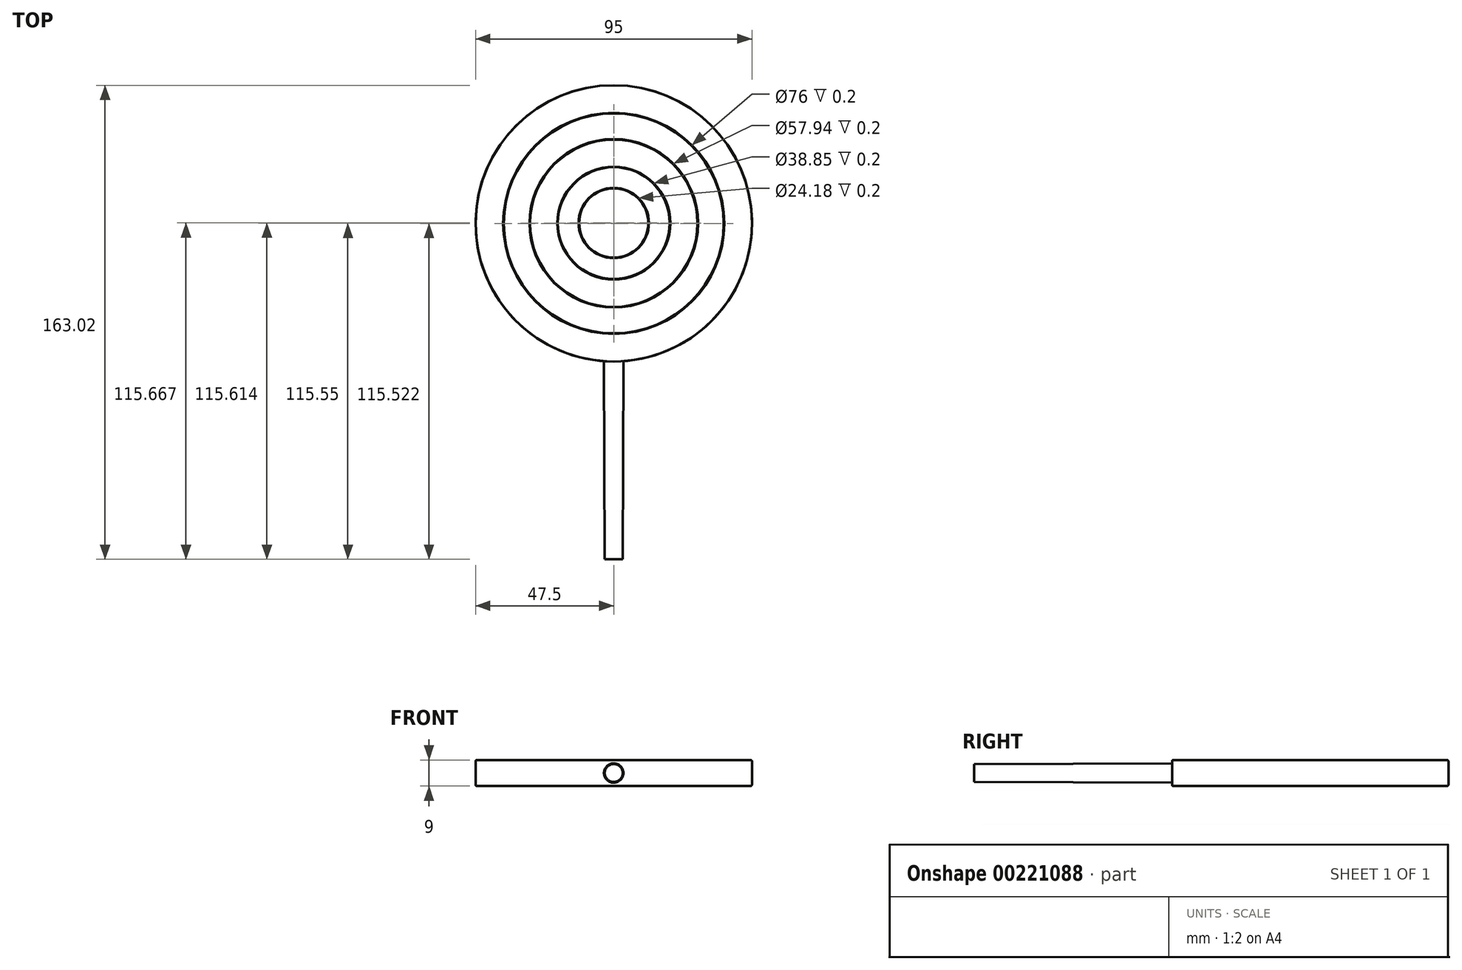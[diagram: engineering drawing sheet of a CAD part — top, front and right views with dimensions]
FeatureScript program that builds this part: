
annotation { "Feature Type Name" : "Feature", "Feature Type Description" : "" }
export const myFeature = defineFeature(function(context is Context, id is Id, definition is map)
    precondition{}
    {
        {
            var Q0;
            Q0=qCreatedBy(makeId("Front.planeOp"),FACE);
            var sketch = newSketch(context, id + "F0", { "sketchPlane" : qUnion([Q0])});
            skCircle(sketch, "E0", {"center": v(0, 1.52) * mm, "radius": 47.5 * mm});
            skLineSegment(sketch, "E1.bottom", {"start": v(35, -115.53) * mm, "end": v(-35, -115.53) * mm});
            skLineSegment(sketch, "E1.top", {"start": v(35, -84.47) * mm, "end": v(-35, -84.47) * mm});
            skLineSegment(sketch, "E1.left", {"start": v(35, -115.53) * mm, "end": v(35, -84.47) * mm});
            skLineSegment(sketch, "E1.right", {"start": v(-35, -115.53) * mm, "end": v(-35, -84.47) * mm});
            skPoint(sketch, "E1.middle", {"position": v(0, -100) * mm});
            skLineSegment(sketch, "E2", {"start": v(0, 71.57) * mm, "end": v(0, -130.11) * mm, "construction": true});
            skPoint(sketch, "E2.endSnap0", {"position": v(0, -115.53) * mm});
            skSolve(sketch);
        }
        {
            var Q0;
            Q0=makeQuery(id+"F0.imprint","IMPRINT",FACE,{"disambiguationData":[TD([[makeQuery(id+"F0.imprint","IMPRINT",EDGE,{"derivedFrom":sQuery(id+"F0.wireOp",EDGE,"E0")}),1.0]])]});
            var Q1;
            Q1=sQuery(id+"F0.wireOp",EDGE,"E0");
            extrude(context, id + "F1", {"entities" : qUnion([Q0]), "surfaceEntities" : qUnion([Q1]), "endBound" : BoundingType.SYMMETRIC, "depth" : 9 * mm});
        }
        {
            var Q0;
            Q0=qCreatedBy(makeId("Top.planeOp"),FACE);
            var sketch = newSketch(context, id + "F2", { "sketchPlane" : qUnion([Q0])});
            skCircle(sketch, "E3", {"center": v(0, 0) * mm, "radius": 3.5 * mm});
            skSolve(sketch);
        }
        {
            var Q0;
            Q0=qSketchRegion(id+"F2",true);
            extrude(context, id + "F3", {"entities" : qUnion([Q0]), "operationType" : NewBodyOperationType.ADD, "oppositeDirection" : true, "depth" : 114 * mm, "hasDraft" : true, "draftAngle" : 0.2 * degree, "draftPullDirection" : true});
        }
        {
            var Q0;
            Q0=makeQuery(id+"F1.opExtrude","CAP_EDGE",EDGE,{"disambiguationData":[OSD([sQuery(id+"F0.wireOp",EDGE,"E0")])],"isStart":false});
            var Q1;
            Q1=makeQuery(id+"F1.opExtrude","CAP_EDGE",EDGE,{"disambiguationData":[OSD([sQuery(id+"F0.wireOp",EDGE,"E0")])],"isStart":true});
            fillet(context, id + "F4", {"entities" : qUnion([Q0, Q1]), "radius" : 0.5 * mm, "tangentPropagation" : true, "allowEdgeOverflow" : false});
        }
        {
            var Q0;
            Q0=makeQuery(id+"F1.opExtrude","CAP_FACE",FACE,{"disambiguationData":[OSD([sQuery(id+"F0.wireOp",EDGE,"E0")])],"isStart":false});
            var sketch = newSketch(context, id + "F5", { "sketchPlane" : qUnion([Q0])});
            skCircle(sketch, "E4", {"center": v(0, 1.52) * mm, "radius": 37.8 * mm});
            skCircle(sketch, "E5.0", {"center": v(0, 1.52) * mm, "radius": 38 * mm});
            skSolve(sketch);
        }
        {
            var Q0;
            Q0=qSketchRegion(id+"F5",true);
            extrude(context, id + "F6", {"entities" : qUnion([Q0]), "operationType" : NewBodyOperationType.REMOVE, "oppositeDirection" : true, "depth" : 0.2 * mm});
        }
        {
            var Q0;
            Q0=makeQuery(id+"F5.imprint","IMPRINT",FACE,{"disambiguationData":[TD([[makeQuery(id+"F5.imprint","IMPRINT",EDGE,{"derivedFrom":sQuery(id+"F5.wireOp",EDGE,"E5.0")}),-1.0]])]});
            var sketch = newSketch(context, id + "F7", { "sketchPlane" : qUnion([Q0])});
            skCircle(sketch, "E6", {"center": v(0, 1.55) * mm, "radius": 28.77 * mm});
            skCircle(sketch, "E7.0", {"center": v(0, 1.55) * mm, "radius": 28.97 * mm});
            skSolve(sketch);
        }
        {
            var Q0;
            Q0=qSketchRegion(id+"F7",true);
            extrude(context, id + "F8", {"entities" : qUnion([Q0]), "operationType" : NewBodyOperationType.REMOVE, "oppositeDirection" : true, "depth" : 0.2 * mm});
        }
        {
            var Q0;
            Q0=makeQuery(id+"F5.imprint","IMPRINT",FACE,{"disambiguationData":[TD([[makeQuery(id+"F5.imprint","IMPRINT",EDGE,{"derivedFrom":sQuery(id+"F5.wireOp",EDGE,"E5.0")}),-1.0]])]});
            var sketch = newSketch(context, id + "F9", { "sketchPlane" : qUnion([Q0])});
            skCircle(sketch, "E8", {"center": v(0, 1.61) * mm, "radius": 19.23 * mm});
            skCircle(sketch, "E9.0", {"center": v(0, 1.61) * mm, "radius": 19.43 * mm});
            skSolve(sketch);
        }
        {
            var Q0;
            Q0=qSketchRegion(id+"F9",true);
            extrude(context, id + "F10", {"entities" : qUnion([Q0]), "operationType" : NewBodyOperationType.REMOVE, "oppositeDirection" : true, "depth" : 0.2 * mm});
        }
        {
            var Q0;
            Q0=makeQuery(id+"F5.imprint","IMPRINT",FACE,{"disambiguationData":[TD([[makeQuery(id+"F5.imprint","IMPRINT",EDGE,{"derivedFrom":sQuery(id+"F5.wireOp",EDGE,"E5.0")}),-1.0]])]});
            var sketch = newSketch(context, id + "F11", { "sketchPlane" : qUnion([Q0])});
            skCircle(sketch, "E10", {"center": v(0, 1.67) * mm, "radius": 11.89 * mm});
            skCircle(sketch, "E11.0", {"center": v(0, 1.67) * mm, "radius": 12.09 * mm});
            skSolve(sketch);
        }
        {
            var Q0;
            Q0=makeQuery(id+"F11.imprint","IMPRINT",FACE,{"disambiguationData":[TD([[makeQuery(id+"F11.imprint","IMPRINT",EDGE,{"derivedFrom":sQuery(id+"F11.wireOp",EDGE,"E10")}),-1.0]])]});
            extrude(context, id + "F12", {"entities" : qUnion([Q0]), "operationType" : NewBodyOperationType.REMOVE, "oppositeDirection" : true, "depth" : 0.2 * mm});
        }
        {
            var Q0;
            Q0=qCreatedBy(makeId("Front.planeOp"),FACE);
            var sketch = newSketch(context, id + "F13", { "sketchPlane" : qUnion([Q0])});
            skLineSegment(sketch, "E12", {"start": v(-133.43, 0) * mm, "end": v(162.94, 0) * mm, "construction": true});
            skSolve(sketch);
        }
        {
            var Q0;
            Q0=makeQuery(id+"F1.opExtrude","SWEPT_BODY",BODY,{"disambiguationData":[OSD([sQuery(id+"F0.wireOp",EDGE,"E0")])]});
            var Q1;
            Q1=sQuery(id+"F13.wireOp",EDGE,"E12");
            transform(context, id + "F14", {"entities" : qUnion([Q0]), "transformType" : TransformType.ROTATION, "transformAxis" : qUnion([Q1]), "angle" : 90 * degree, "oppositeDirection" : true, "makeCopy" : false});
        }
    });
